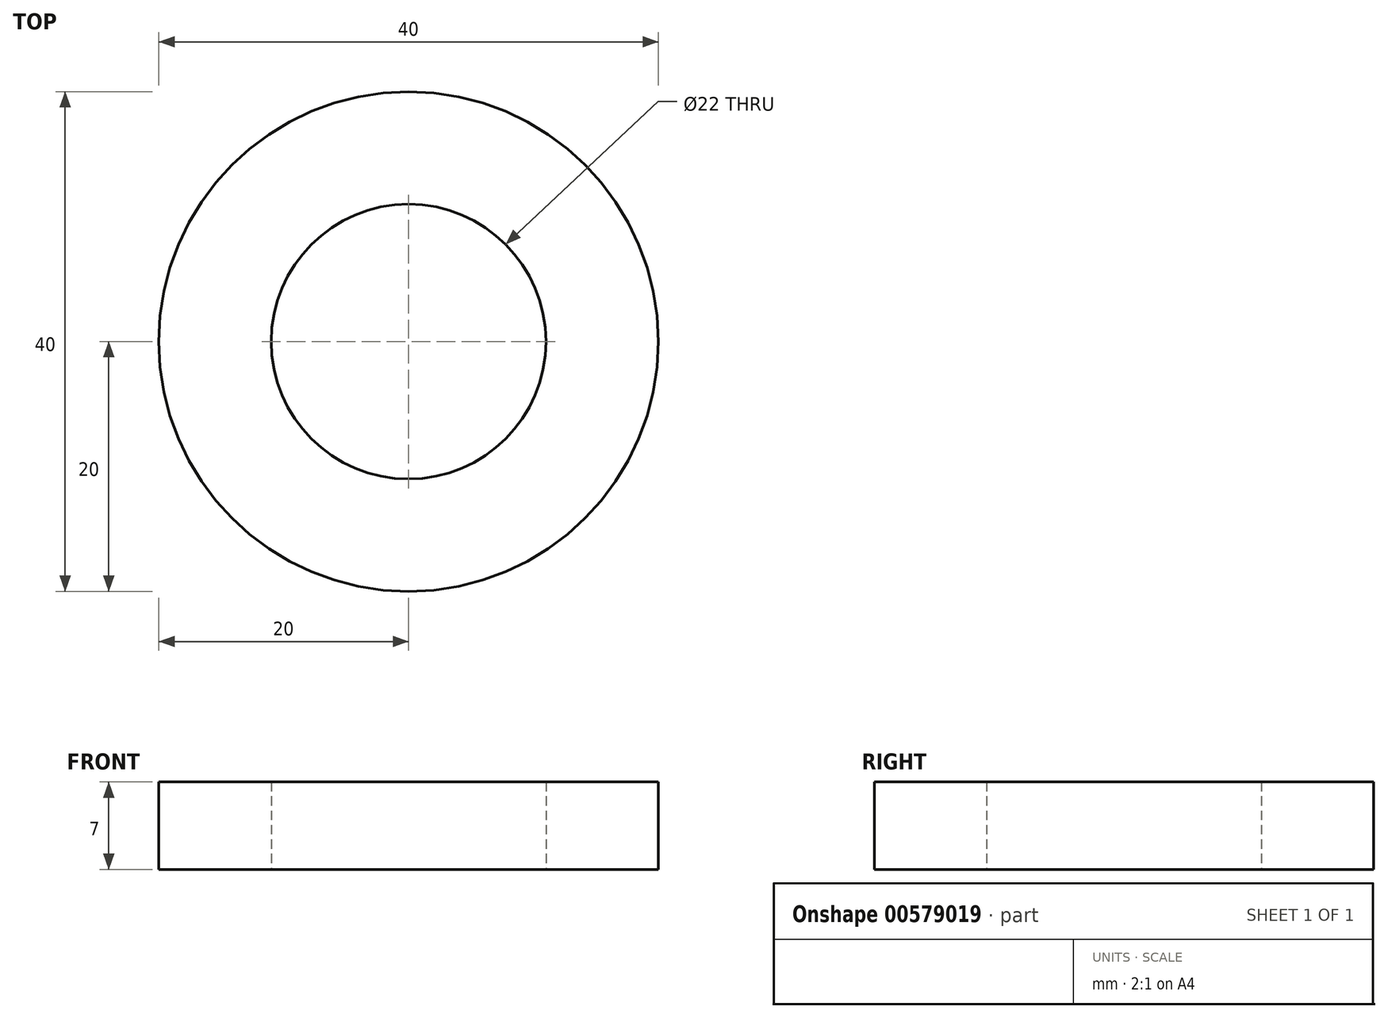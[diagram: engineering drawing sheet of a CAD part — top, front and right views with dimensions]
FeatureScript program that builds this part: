
annotation { "Feature Type Name" : "Feature", "Feature Type Description" : "" }
export const myFeature = defineFeature(function(context is Context, id is Id, definition is map)
    precondition{}
    {
        {
            var Q0;
            Q0=qCreatedBy(makeId("Top.planeOp"),FACE);
            var sketch = newSketch(context, id + "F0", { "sketchPlane" : qUnion([Q0])});
            skCircle(sketch, "E0", {"center": v(0, 0) * mm, "radius": 11 * mm});
            skCircle(sketch, "E1", {"center": v(0, 0) * mm, "radius": 20 * mm});
            skSolve(sketch);
        }
        {
            var Q0;
            Q0=makeQuery(id+"F0.imprint","IMPRINT",FACE,{"disambiguationData":[TD([[makeQuery(id+"F0.imprint","IMPRINT",EDGE,{"derivedFrom":sQuery(id+"F0.wireOp",EDGE,"E0")}),-1.0]])]});
            extrude(context, id + "F1", {"entities" : qUnion([Q0]), "depth" : 7 * mm, "offsetDistance" : 25 * mm});
        }
    });
